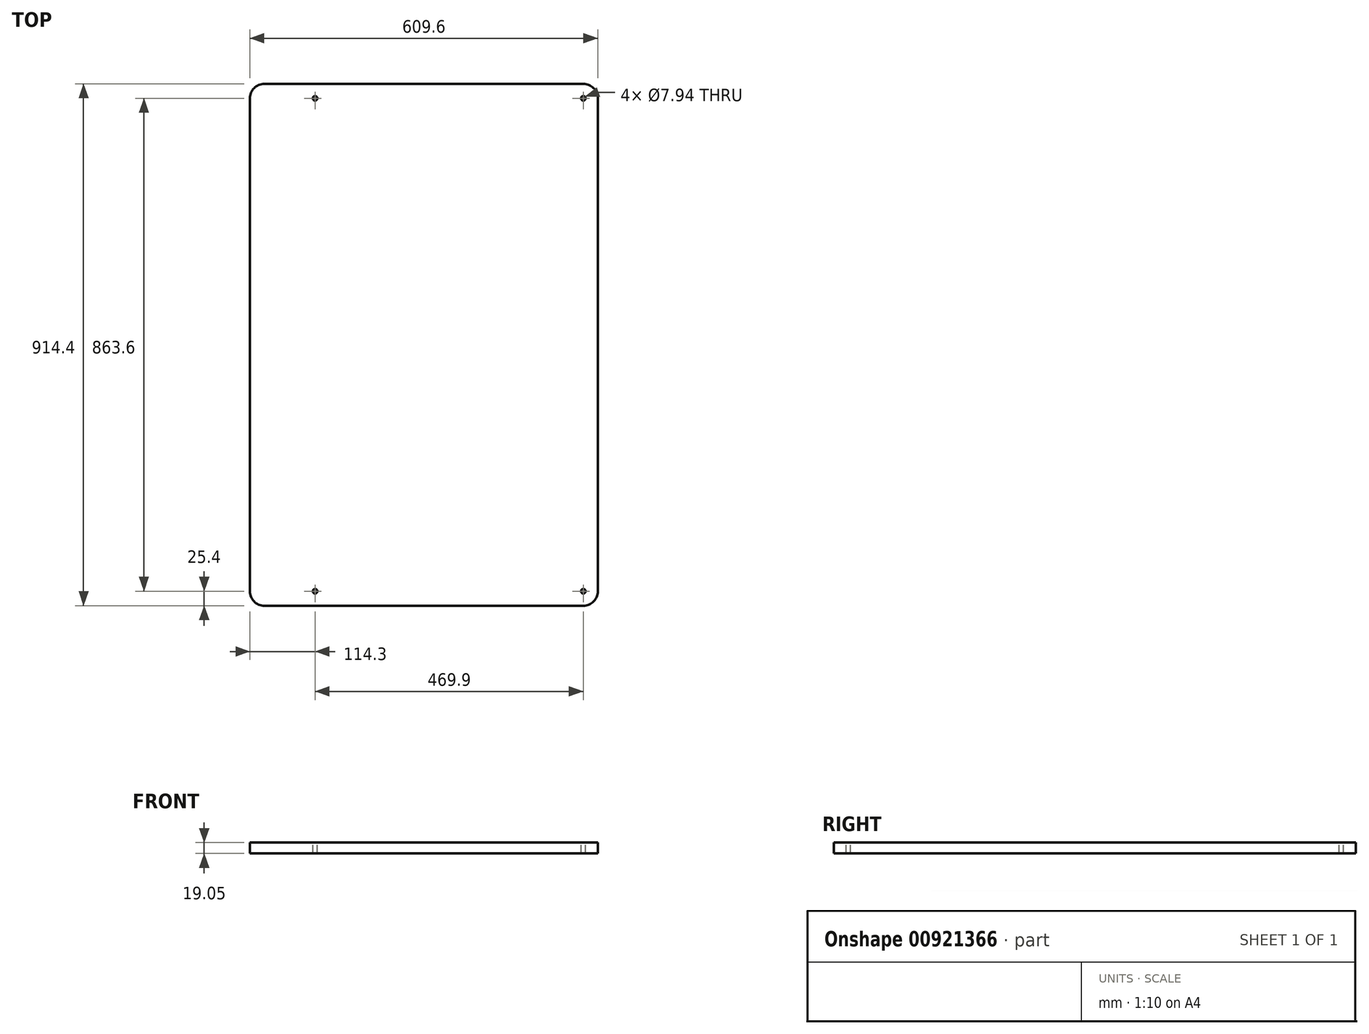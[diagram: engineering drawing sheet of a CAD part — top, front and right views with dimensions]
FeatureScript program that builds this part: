
annotation { "Feature Type Name" : "Feature", "Feature Type Description" : "" }
export const myFeature = defineFeature(function(context is Context, id is Id, definition is map)
    precondition{}
    {
        {
            var Q0;
            Q0=qCreatedBy(makeId("Top.planeOp"),FACE);
            var sketch = newSketch(context, id + "F0", { "sketchPlane" : qUnion([Q0])});
            skLineSegment(sketch, "E0.bottom", {"start": v(304.8, -457.2) * mm, "end": v(-304.8, -457.2) * mm});
            skLineSegment(sketch, "E0.top", {"start": v(304.8, 457.2) * mm, "end": v(-304.8, 457.2) * mm});
            skLineSegment(sketch, "E0.left", {"start": v(304.8, -457.2) * mm, "end": v(304.8, 457.2) * mm});
            skLineSegment(sketch, "E0.right", {"start": v(-304.8, -457.2) * mm, "end": v(-304.8, 457.2) * mm});
            skLineSegment(sketch, "E1", {"start": v(304.8, -457.2) * mm, "end": v(-304.8, 457.2) * mm, "construction": true});
            skSolve(sketch);
        }
        {
            var Q0;
            Q0 = qSketchRegion(id + "F0", true);
            extrude(context, id + "F1", {"entities" : qUnion([Q0]), "oppositeDirection" : true, "depth" : 19.05 * mm, "offsetDistance" : 25.4 * mm});
        }
        {
            var Q0;
            Q0=makeQuery(id+"F1.opExtrude","SWEPT_EDGE",EDGE,{"disambiguationData":[OSD([sQuery(id+"F0.wireOp",EDGE,"E0.bottom"),sQuery(id+"F0.wireOp",EDGE,"E0.right")])]});
            var Q1;
            Q1=makeQuery(id+"F1.opExtrude","SWEPT_EDGE",EDGE,{"disambiguationData":[OSD([sQuery(id+"F0.wireOp",EDGE,"E0.top"),sQuery(id+"F0.wireOp",EDGE,"E0.right")])]});
            var Q2;
            Q2=makeQuery(id+"F1.opExtrude","SWEPT_EDGE",EDGE,{"disambiguationData":[OSD([sQuery(id+"F0.wireOp",EDGE,"E0.top"),sQuery(id+"F0.wireOp",EDGE,"E0.left")])]});
            var Q3;
            Q3=makeQuery(id+"F1.opExtrude","SWEPT_EDGE",EDGE,{"disambiguationData":[OSD([sQuery(id+"F0.wireOp",EDGE,"E0.bottom"),sQuery(id+"F0.wireOp",EDGE,"E0.left")])]});
            fillet(context, id + "F2", {"entities" : qUnion([Q0, Q1, Q2, Q3]), "radius" : 25.4 * mm, "tangentPropagation" : true, "allowEdgeOverflow" : false});
        }
        {
            var Q0;
            Q0=makeQuery(id+"F1.opExtrude","CAP_FACE",FACE,{"disambiguationData":[OSD([sQuery(id+"F0.wireOp",EDGE,"E0.bottom"),sQuery(id+"F0.wireOp",EDGE,"E0.top"),sQuery(id+"F0.wireOp",EDGE,"E0.left"),sQuery(id+"F0.wireOp",EDGE,"E0.right")])],"isStart":true});
            var sketch = newSketch(context, id + "F3", { "sketchPlane" : qUnion([Q0])});
            skLineSegment(sketch, "E2.bottom", {"start": v(-190.5, -431.8) * mm, "end": v(279.4, -431.8) * mm, "construction": true});
            skLineSegment(sketch, "E2.top", {"start": v(-190.5, 431.8) * mm, "end": v(279.4, 431.8) * mm, "construction": true});
            skLineSegment(sketch, "E2.left", {"start": v(-190.5, -431.8) * mm, "end": v(-190.5, 431.8) * mm, "construction": true});
            skLineSegment(sketch, "E2.right", {"start": v(279.4, -431.8) * mm, "end": v(279.4, 431.8) * mm, "construction": true});
            skCircle(sketch, "E3", {"center": v(-190.5, -431.8) * mm, "radius": 3.97 * mm});
            skCircle(sketch, "E4", {"center": v(279.4, -431.8) * mm, "radius": 3.97 * mm});
            skCircle(sketch, "E5", {"center": v(279.4, 431.8) * mm, "radius": 3.97 * mm});
            skCircle(sketch, "E6", {"center": v(-190.5, 431.8) * mm, "radius": 3.97 * mm});
            skSolve(sketch);
        }
        {
            var Q0;
            Q0 = qSketchRegion(id + "F3", true);
            extrude(context, id + "F4", {"entities" : qUnion([Q0]), "operationType" : NewBodyOperationType.REMOVE, "endBound" : BoundingType.THROUGH_ALL, "oppositeDirection" : true, "depth" : 25.4 * mm, "offsetDistance" : 25.4 * mm});
        }
    });
